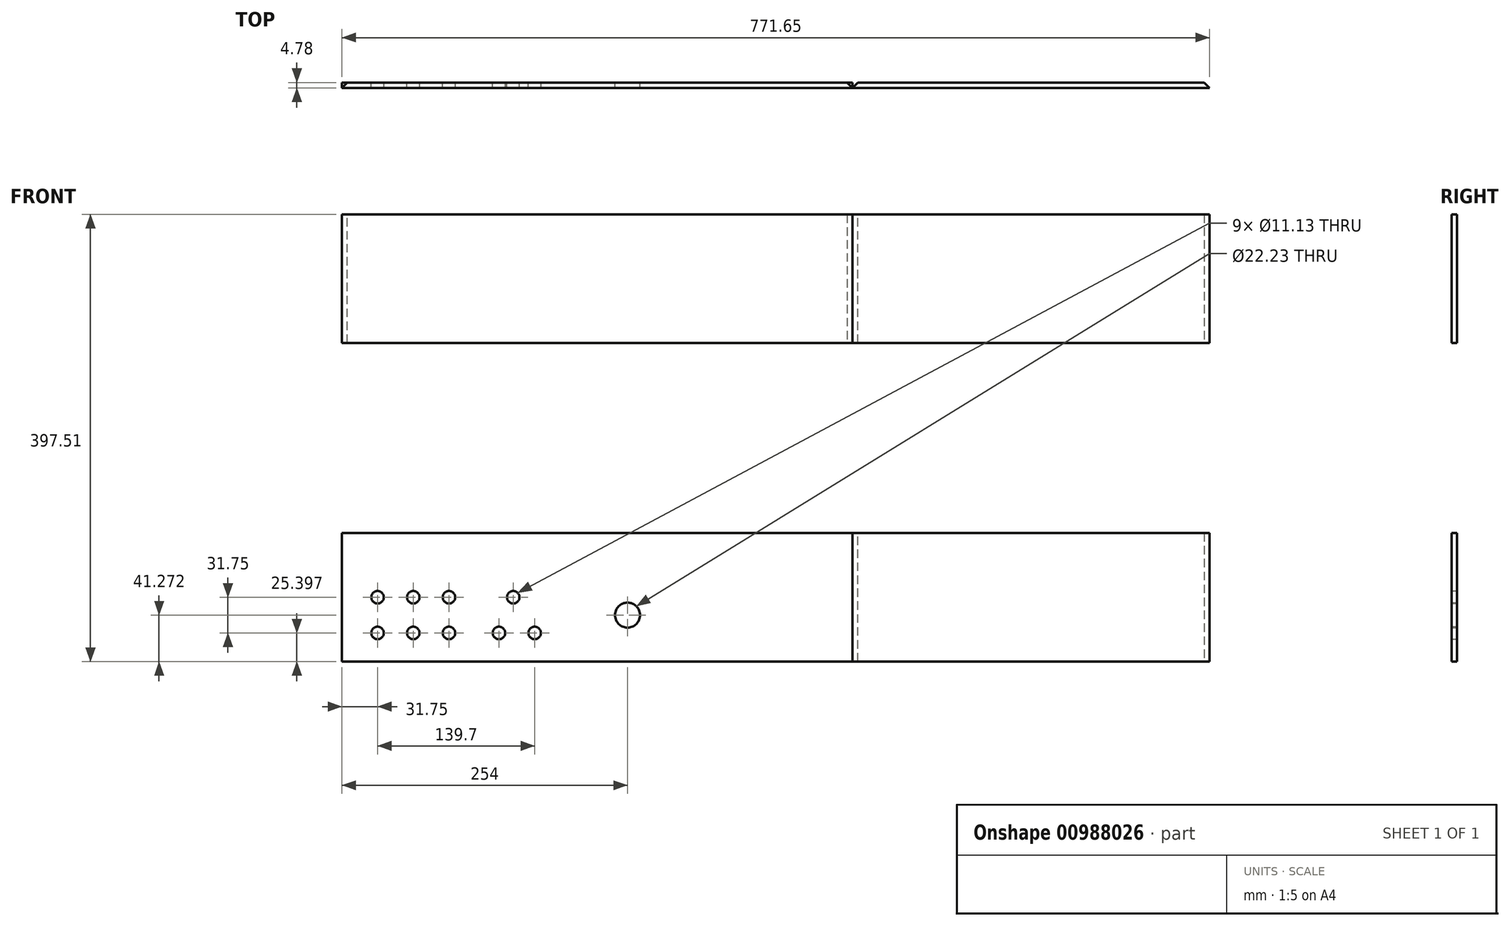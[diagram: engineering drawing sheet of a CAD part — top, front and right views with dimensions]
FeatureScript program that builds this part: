
annotation { "Feature Type Name" : "Feature", "Feature Type Description" : "" }
export const myFeature = defineFeature(function(context is Context, id is Id, definition is map)
    precondition{}
    {
        {
            var Q0;
            Q0=qCreatedBy(makeId("Front.planeOp"),FACE);
            var sketch = newSketch(context, id + "F0", { "sketchPlane" : qUnion([Q0])});
            skLineSegment(sketch, "E0.bottom", {"start": v(-189.37, 59.29) * mm, "end": v(264.66, 59.29) * mm});
            skLineSegment(sketch, "E0.top", {"start": v(-189.37, -55.01) * mm, "end": v(264.66, -55.01) * mm});
            skLineSegment(sketch, "E0.left", {"start": v(-189.37, 59.29) * mm, "end": v(-189.37, -55.01) * mm});
            skLineSegment(sketch, "E0.right", {"start": v(264.66, 59.29) * mm, "end": v(264.66, -55.01) * mm});
            skCircle(sketch, "E1", {"center": v(-157.62, -29.61) * mm, "radius": 5.56 * mm});
            skCircle(sketch, "E2", {"center": v(-125.87, -29.61) * mm, "radius": 5.56 * mm});
            skCircle(sketch, "E3", {"center": v(-94.12, -29.61) * mm, "radius": 5.56 * mm});
            skCircle(sketch, "E4", {"center": v(-17.92, -29.61) * mm, "radius": 5.56 * mm});
            skCircle(sketch, "E5", {"center": v(-49.67, -29.61) * mm, "radius": 5.56 * mm});
            skCircle(sketch, "E6", {"center": v(-157.62, 2.14) * mm, "radius": 5.56 * mm});
            skCircle(sketch, "E7", {"center": v(-125.87, 2.14) * mm, "radius": 5.56 * mm});
            skCircle(sketch, "E8", {"center": v(-94.12, 2.14) * mm, "radius": 5.56 * mm});
            skCircle(sketch, "E9", {"center": v(-36.97, 2.14) * mm, "radius": 5.56 * mm});
            skPoint(sketch, "E10", {"position": v(-157.62, -3.51) * mm});
            skCircle(sketch, "E11", {"center": v(64.63, -13.74) * mm, "radius": 11.11 * mm});
            skLineSegment(sketch, "E12", {"start": v(35.92, -13.74) * mm, "end": v(93.64, -13.74) * mm, "construction": true});
            skLineSegment(sketch, "E13.bottom", {"start": v(-189.37, 342.5) * mm, "end": v(264.66, 342.5) * mm});
            skLineSegment(sketch, "E13.top", {"start": v(-189.37, 228.2) * mm, "end": v(264.66, 228.2) * mm});
            skLineSegment(sketch, "E13.left", {"start": v(-189.37, 342.5) * mm, "end": v(-189.37, 228.2) * mm});
            skLineSegment(sketch, "E13.right", {"start": v(264.66, 342.5) * mm, "end": v(264.66, 228.2) * mm});
            skLineSegment(sketch, "E14.bottom", {"start": v(264.78, 59.29) * mm, "end": v(582.28, 59.29) * mm});
            skLineSegment(sketch, "E14.top", {"start": v(264.78, -55.01) * mm, "end": v(582.28, -55.01) * mm});
            skLineSegment(sketch, "E14.left", {"start": v(264.78, 59.29) * mm, "end": v(264.78, -55.01) * mm});
            skLineSegment(sketch, "E14.right", {"start": v(582.28, 59.29) * mm, "end": v(582.28, -55.01) * mm});
            skLineSegment(sketch, "E15.bottom", {"start": v(264.71, 342.5) * mm, "end": v(582.21, 342.5) * mm});
            skLineSegment(sketch, "E15.top", {"start": v(264.71, 228.2) * mm, "end": v(582.21, 228.2) * mm});
            skLineSegment(sketch, "E15.left", {"start": v(264.71, 342.5) * mm, "end": v(264.71, 228.2) * mm});
            skLineSegment(sketch, "E15.right", {"start": v(582.21, 342.5) * mm, "end": v(582.21, 228.2) * mm});
            skPoint(sketch, "E16", {"position": v(-189.37, 2.14) * mm});
            skLineSegment(sketch, "E17", {"start": v(-23.53, 2.14) * mm, "end": v(-172.07, 2.14) * mm, "construction": true});
            skLineSegment(sketch, "E18", {"start": v(-6.27, -29.61) * mm, "end": v(-172.82, -29.61) * mm, "construction": true});
            skSolve(sketch);
        }
        {
            var Q0;
            Q0=makeQuery(id+"F0.imprint","IMPRINT",FACE,{"disambiguationData":[TD([[makeQuery(id+"F0.imprint","IMPRINT",EDGE,{"derivedFrom":sQuery(id+"F0.wireOp",EDGE,"545v1GDX-f99N-rFf9-VLLV-KYLq5Sl5wzxr.bottom")}),1.0]])]});
            var Q1;
            Q1=makeQuery(id+"F0.imprint","IMPRINT",FACE,{"disambiguationData":[TD([[makeQuery(id+"F0.imprint","IMPRINT",EDGE,{"derivedFrom":sQuery(id+"F0.wireOp",EDGE,"E0.bottom")}),-1.0]])]});
            var Q2;
            Q2=makeQuery(id+"F0.imprint","IMPRINT",FACE,{"disambiguationData":[TD([[makeQuery(id+"F0.imprint","IMPRINT",EDGE,{"derivedFrom":sQuery(id+"F0.wireOp",EDGE,"mhuvXMkW-k5QU-e71L-HkeC-ZcxIXtxDrWED.bottom")}),-1.0]])]});
            var Q3;
            Q3=makeQuery(id+"F0.imprint","IMPRINT",FACE,{"disambiguationData":[TD([[makeQuery(id+"F0.imprint","IMPRINT",EDGE,{"derivedFrom":sQuery(id+"F0.wireOp",EDGE,"E13.bottom")}),-1.0]])]});
            var Q4;
            Q4=makeQuery(id+"F0.imprint","IMPRINT",FACE,{"disambiguationData":[TD([[makeQuery(id+"F0.imprint","IMPRINT",EDGE,{"derivedFrom":sQuery(id+"F0.wireOp",EDGE,"c9704ad7-6529-4927-9bfb-224757631aca.bottom")}),-1.0]])]});
            var Q5;
            Q5=makeQuery(id+"F0.imprint","IMPRINT",FACE,{"disambiguationData":[TD([[makeQuery(id+"F0.imprint","IMPRINT",EDGE,{"derivedFrom":sQuery(id+"F0.wireOp",EDGE,"E14.bottom")}),-1.0]])]});
            var Q6;
            Q6=makeQuery(id+"F0.imprint","IMPRINT",FACE,{"disambiguationData":[TD([[makeQuery(id+"F0.imprint","IMPRINT",EDGE,{"derivedFrom":sQuery(id+"F0.wireOp",EDGE,"E15.bottom")}),-1.0]])]});
            extrude(context, id + "F1", {"entities" : qUnion([Q0, Q1, Q2, Q3, Q4, Q5, Q6]), "depth" : 4.78 * mm, "offsetDistance" : 25.4 * mm});
        }
        {
            var Q0;
            Q0=makeQuery(id+"F1.opExtrude","CAP_EDGE",EDGE,{"disambiguationData":[OSD([sQuery(id+"F0.wireOp",EDGE,"E13.right")])],"isStart":true});
            var Q1;
            Q1=makeQuery(id+"F1.opExtrude","CAP_EDGE",EDGE,{"disambiguationData":[OSD([sQuery(id+"F0.wireOp",EDGE,"nuOChE4Q-GeEQ-fmZ5-sQOg-7unvAZLmPYGS.right")])],"isStart":true});
            var Q2;
            Q2=makeQuery(id+"F1.opExtrude","CAP_EDGE",EDGE,{"disambiguationData":[OSD([sQuery(id+"F0.wireOp",EDGE,"nuOChE4Q-GeEQ-fmZ5-sQOg-7unvAZLmPYGS.left")])],"isStart":true});
            var Q3;
            Q3=makeQuery(id+"F1.opExtrude","CAP_EDGE",EDGE,{"disambiguationData":[OSD([sQuery(id+"F0.wireOp",EDGE,"B0YEpUnT-bHue-zKPS-oTuu-Fwo21ukIs0fQ.right")])],"isStart":true});
            var Q4;
            Q4=makeQuery(id+"F1.opExtrude","CAP_EDGE",EDGE,{"disambiguationData":[OSD([sQuery(id+"F0.wireOp",EDGE,"E0.right")])],"isStart":true});
            var Q5;
            Q5=makeQuery(id+"F1.opExtrude","CAP_EDGE",EDGE,{"disambiguationData":[OSD([sQuery(id+"F0.wireOp",EDGE,"E0.left")])],"isStart":true});
            var Q6;
            Q6=makeQuery(id+"F1.opExtrude","CAP_EDGE",EDGE,{"disambiguationData":[OSD([sQuery(id+"F0.wireOp",EDGE,"6243fc9e-a803-4f9e-ac64-01b7eac565c9.left")])],"isStart":true});
            var Q7;
            Q7=makeQuery(id+"F1.opExtrude","CAP_EDGE",EDGE,{"disambiguationData":[OSD([sQuery(id+"F0.wireOp",EDGE,"545v1GDX-f99N-rFf9-VLLV-KYLq5Sl5wzxr.right")])],"isStart":true});
            var Q8;
            Q8=makeQuery(id+"F1.opExtrude","CAP_EDGE",EDGE,{"disambiguationData":[OSD([sQuery(id+"F0.wireOp",EDGE,"E13.left")])],"isStart":true});
            var Q9;
            Q9=makeQuery(id+"F1.opExtrude","CAP_EDGE",EDGE,{"disambiguationData":[OSD([sQuery(id+"F0.wireOp",EDGE,"mhuvXMkW-k5QU-e71L-HkeC-ZcxIXtxDrWED.right")])],"isStart":true});
            var Q10;
            Q10=makeQuery(id+"F1.opExtrude","CAP_EDGE",EDGE,{"disambiguationData":[OSD([sQuery(id+"F0.wireOp",EDGE,"a2b257b9-3a88-4484-a7b0-7f61f39d5811.right")])],"isStart":true});
            var Q11;
            Q11=makeQuery(id+"F1.opExtrude","CAP_EDGE",EDGE,{"disambiguationData":[OSD([sQuery(id+"F0.wireOp",EDGE,"c9704ad7-6529-4927-9bfb-224757631aca.right")])],"isStart":true});
            var Q12;
            Q12=makeQuery(id+"F1.opExtrude","CAP_EDGE",EDGE,{"disambiguationData":[OSD([sQuery(id+"F0.wireOp",EDGE,"E14.right")])],"isStart":true});
            var Q13;
            Q13=makeQuery(id+"F1.opExtrude","CAP_EDGE",EDGE,{"disambiguationData":[OSD([sQuery(id+"F0.wireOp",EDGE,"E14.left")])],"isStart":true});
            var Q14;
            Q14=makeQuery(id+"F1.opExtrude","CAP_EDGE",EDGE,{"disambiguationData":[OSD([sQuery(id+"F0.wireOp",EDGE,"E15.left")])],"isStart":true});
            var Q15;
            Q15=makeQuery(id+"F1.opExtrude","CAP_EDGE",EDGE,{"disambiguationData":[OSD([sQuery(id+"F0.wireOp",EDGE,"E15.right")])],"isStart":true});
            chamfer(context, id + "F2", {"entities" : qUnion([Q0, Q1, Q2, Q3, Q4, Q5, Q6, Q7, Q8, Q9, Q10, Q11, Q12, Q13, Q14, Q15]), "width" : 4.78 * mm, "tangentPropagation" : true});
        }
    });
